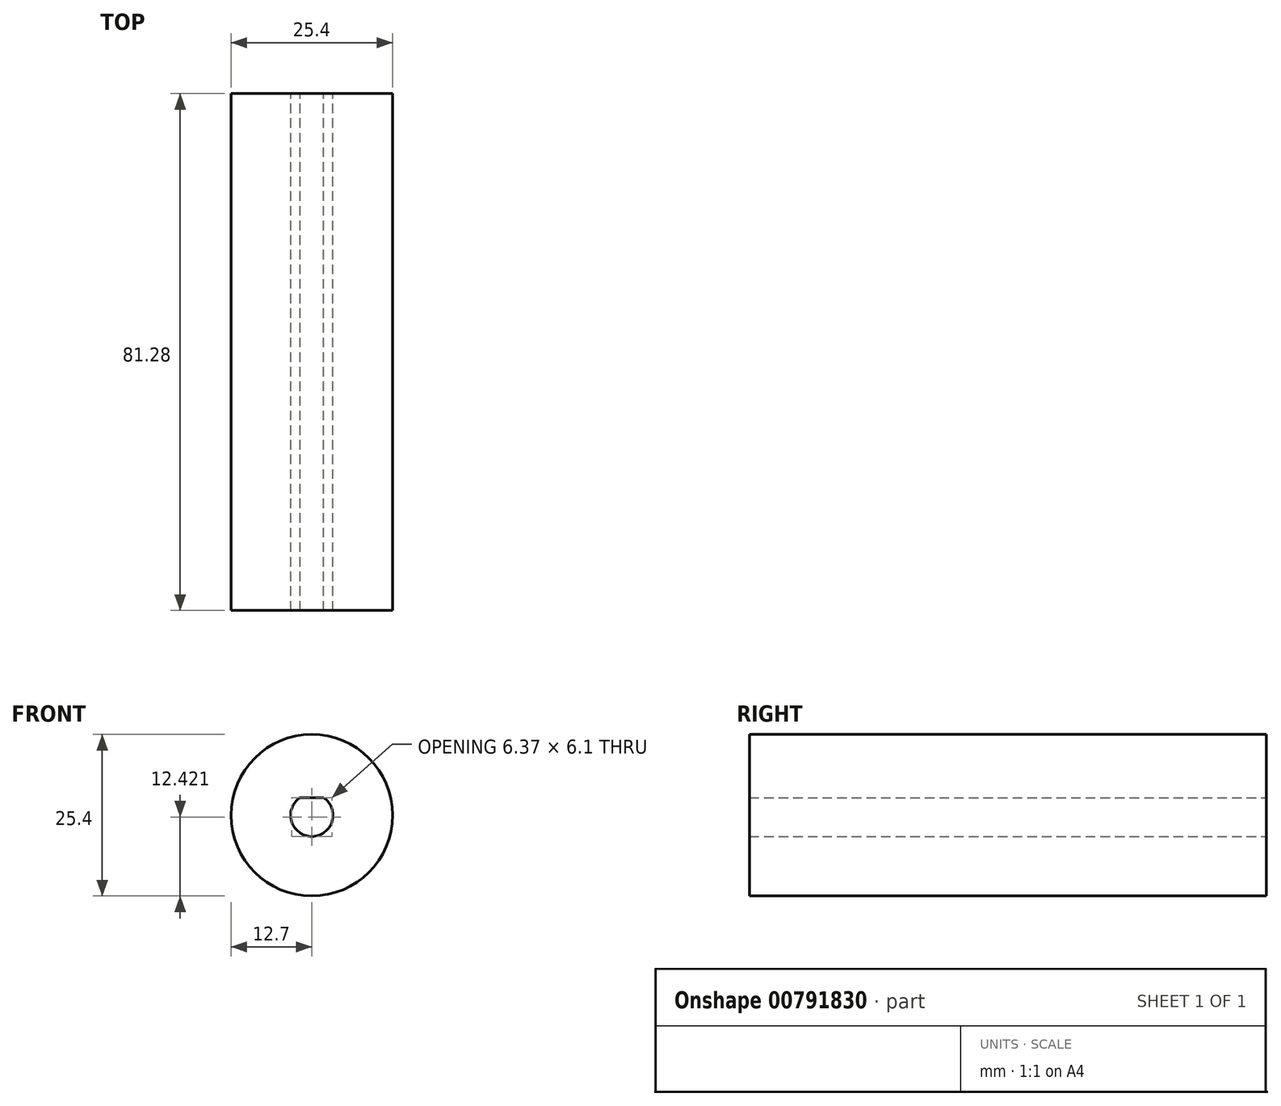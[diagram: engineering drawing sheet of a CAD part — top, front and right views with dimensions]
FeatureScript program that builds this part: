
annotation { "Feature Type Name" : "Feature", "Feature Type Description" : "" }
export const myFeature = defineFeature(function(context is Context, id is Id, definition is map)
    precondition{}
    {
        {
            var Q0;
            Q0=qCreatedBy(makeId("Front.planeOp"),FACE);
            var sketch = newSketch(context, id + "F0", { "sketchPlane" : qUnion([Q0])});
            skArc(sketch, "E0", {"start": v(-1.85, 2.77) * mm, "mid": v(0, -3.33) * mm, "end": v(1.85, 2.77) * mm});
            skCircle(sketch, "E1", {"center": v(0, 0) * mm, "radius": 12.7 * mm});
            skLineSegment(sketch, "E2", {"start": v(-1.85, 2.77) * mm, "end": v(1.85, 2.77) * mm});
            skSolve(sketch);
        }
        {
            var Q0;
            Q0=makeQuery(id+"F0.imprint","IMPRINT",FACE,{"disambiguationData":[TD([[makeQuery(id+"F0.imprint","IMPRINT",EDGE,{"derivedFrom":sQuery(id+"F0.wireOp",EDGE,"E0")}),-1.0]])]});
            extrude(context, id + "F1", {"entities" : qUnion([Q0]), "depth" : 81.28 * mm, "offsetDistance" : 25.4 * mm});
        }
    });
